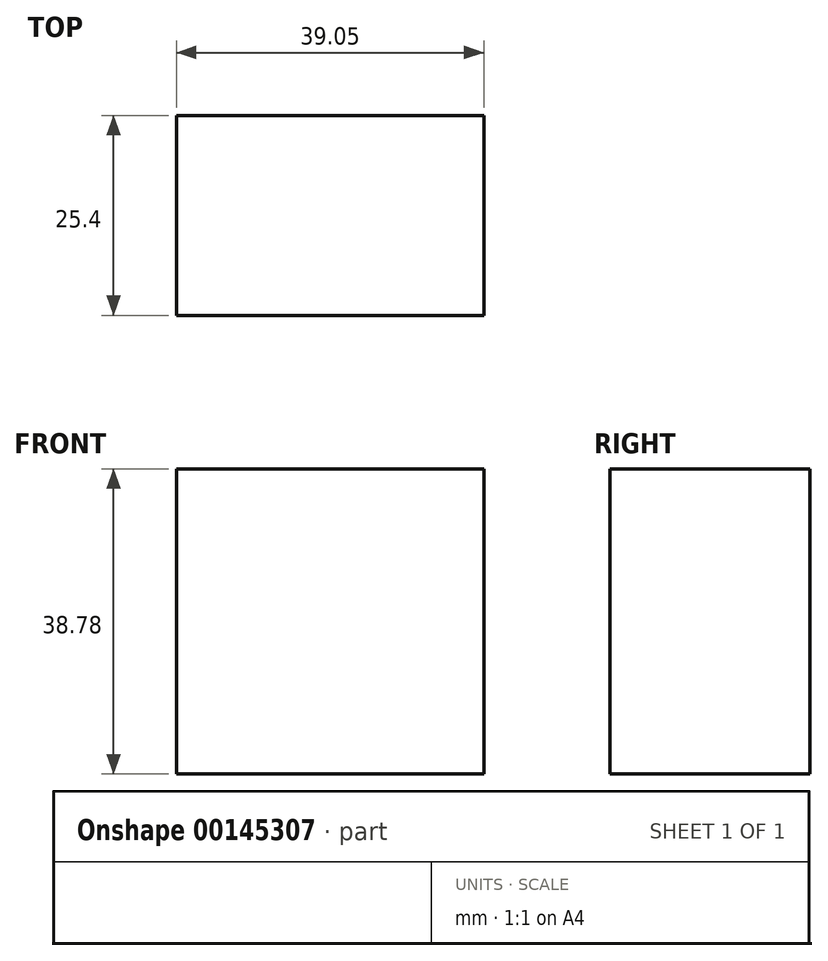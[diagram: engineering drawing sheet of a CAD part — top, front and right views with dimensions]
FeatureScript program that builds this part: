
annotation { "Feature Type Name" : "Feature", "Feature Type Description" : "" }
export const myFeature = defineFeature(function(context is Context, id is Id, definition is map)
    precondition{}
    {
        {
            var Q0;
            Q0=qCreatedBy(makeId("Front.planeOp"),FACE);
            var sketch = newSketch(context, id + "F0", { "sketchPlane" : qUnion([Q0])});
            skLineSegment(sketch, "E0", {"start": v(0, 0) * mm, "end": v(0, 38.78) * mm});
            skLineSegment(sketch, "E1", {"start": v(0, 38.78) * mm, "end": v(39.05, 38.78) * mm});
            skLineSegment(sketch, "E2", {"start": v(39.05, 38.78) * mm, "end": v(39.05, 0) * mm});
            skLineSegment(sketch, "E3", {"start": v(39.05, 0) * mm, "end": v(0, 0) * mm});
            skSolve(sketch);
        }
        {
            var Q0;
            Q0=makeQuery(id+"F0.imprint","IMPRINT",FACE,{"disambiguationData":[TD([[makeQuery(id+"F0.imprint","IMPRINT",EDGE,{"derivedFrom":sQuery(id+"F0.wireOp",EDGE,"E0")}),-1.0]])]});
            extrude(context, id + "F1", {"entities" : qUnion([Q0]), "endBound" : BoundingType.SYMMETRIC, "depth" : 25.4 * mm});
        }
    });
